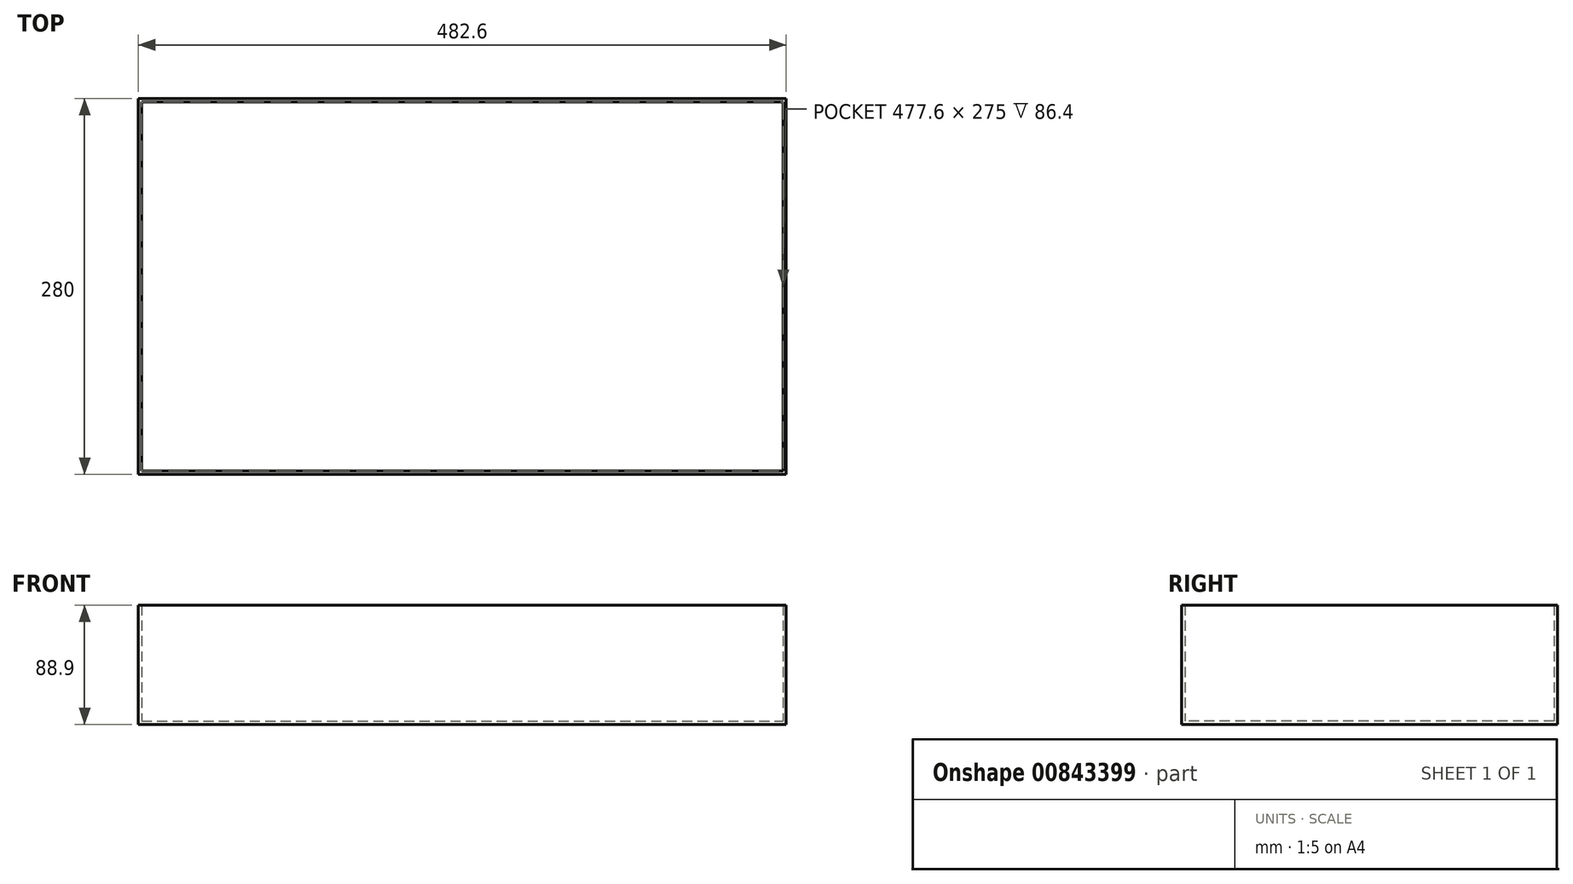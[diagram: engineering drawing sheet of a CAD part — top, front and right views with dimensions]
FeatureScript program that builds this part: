
annotation { "Feature Type Name" : "Feature", "Feature Type Description" : "" }
export const myFeature = defineFeature(function(context is Context, id is Id, definition is map)
    precondition{}
    {
        {
            var Q0;
            Q0=qCreatedBy(makeId("Top.planeOp"),FACE);
            var sketch = newSketch(context, id + "F0", { "sketchPlane" : qUnion([Q0])});
            skLineSegment(sketch, "E0.bottom", {"start": v(-95.8, 214.77) * mm, "end": v(386.8, 214.77) * mm});
            skLineSegment(sketch, "E0.top", {"start": v(-95.8, -65.23) * mm, "end": v(386.8, -65.23) * mm});
            skLineSegment(sketch, "E0.left", {"start": v(-95.8, 214.77) * mm, "end": v(-95.8, -65.23) * mm});
            skLineSegment(sketch, "E0.right", {"start": v(386.8, 214.77) * mm, "end": v(386.8, -65.23) * mm});
            skSolve(sketch);
        }
        {
            var Q0;
            Q0=makeQuery(id+"F0.imprint","IMPRINT",FACE,{"disambiguationData":[TD([[makeQuery(id+"F0.imprint","IMPRINT",EDGE,{"derivedFrom":sQuery(id+"F0.wireOp",EDGE,"E0.bottom")}),-1.0]])]});
            extrude(context, id + "F1", {"entities" : qUnion([Q0]), "surfaceOperationType" : NewSurfaceOperationType.ADD, "depth" : 88.9 * mm, "offsetDistance" : 25 * mm});
        }
        {
            var Q0;
            Q0=makeQuery(id+"F1.opExtrude","CAP_FACE",FACE,{"disambiguationData":[OSD([sQuery(id+"F0.wireOp",EDGE,"E0.bottom"),sQuery(id+"F0.wireOp",EDGE,"E0.top"),sQuery(id+"F0.wireOp",EDGE,"E0.left"),sQuery(id+"F0.wireOp",EDGE,"E0.right")])],"isStart":false});
            shell(context, id + "F2", {"entities" : qUnion([Q0]), "thickness" : 2.5 * mm});
        }
    });
